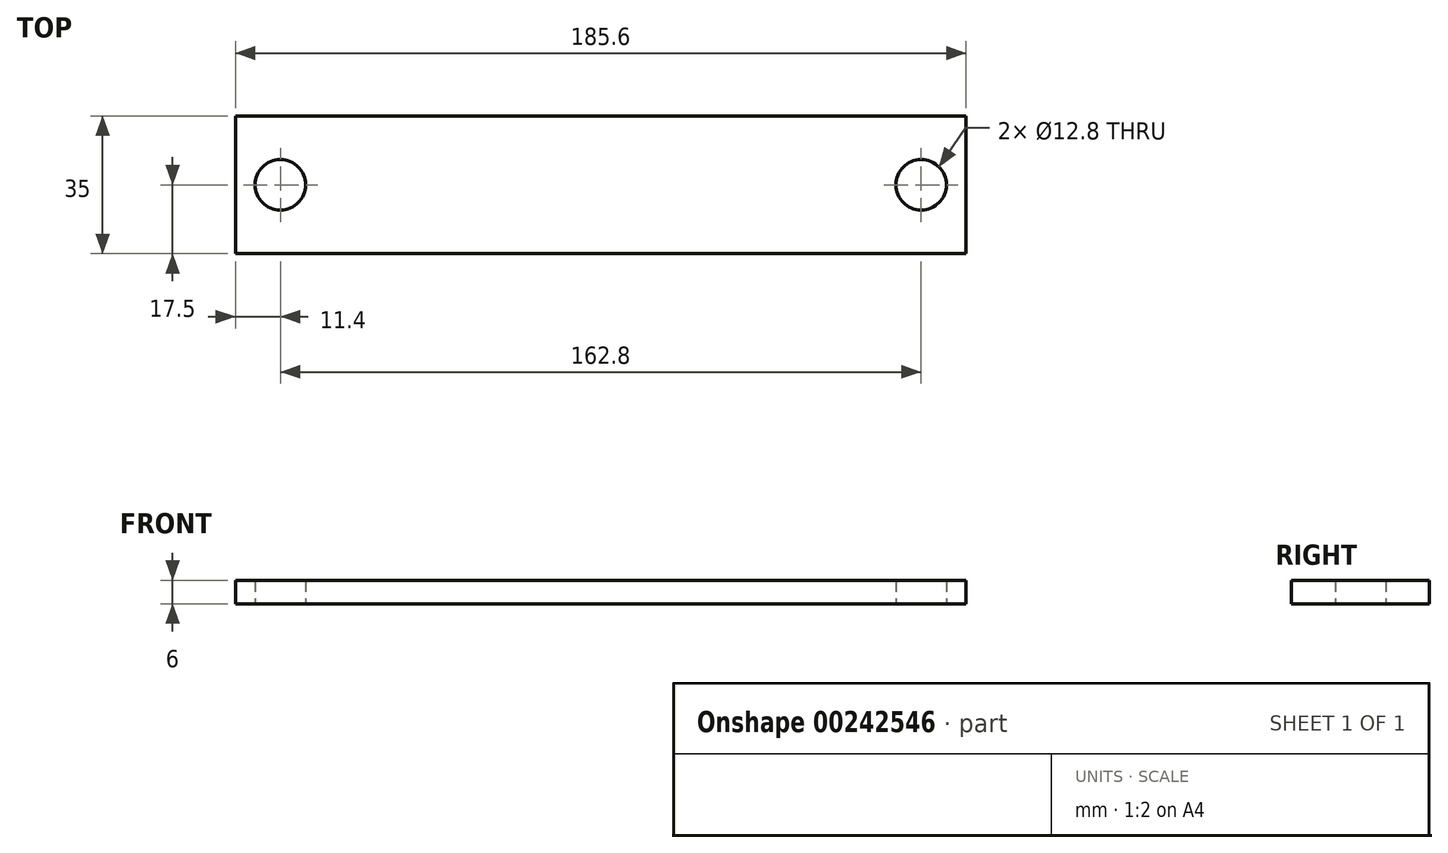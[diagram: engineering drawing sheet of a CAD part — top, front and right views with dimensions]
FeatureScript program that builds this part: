
annotation { "Feature Type Name" : "Feature", "Feature Type Description" : "" }
export const myFeature = defineFeature(function(context is Context, id is Id, definition is map)
    precondition{}
    {
        {
            var Q0;
            Q0=qCreatedBy(makeId("Top.planeOp"),FACE);
            var sketch = newSketch(context, id + "F0", { "sketchPlane" : qUnion([Q0])});
            skLineSegment(sketch, "E0.bottom", {"start": v(92.8, -17.5) * mm, "end": v(-92.8, -17.5) * mm});
            skLineSegment(sketch, "E0.top", {"start": v(92.8, 17.5) * mm, "end": v(-92.8, 17.5) * mm});
            skLineSegment(sketch, "E0.left", {"start": v(92.8, -17.5) * mm, "end": v(92.8, 17.5) * mm});
            skLineSegment(sketch, "E0.right", {"start": v(-92.8, -17.5) * mm, "end": v(-92.8, 17.5) * mm});
            skPoint(sketch, "E0.middle", {"position": v(0, 0) * mm});
            skCircle(sketch, "E1", {"center": v(-81.4, 0) * mm, "radius": 6.4 * mm});
            skCircle(sketch, "E2", {"center": v(81.4, 0) * mm, "radius": 6.4 * mm});
            skSolve(sketch);
        }
        {
            var Q0;
            Q0=makeQuery(id+"F0.imprint","IMPRINT",FACE,{"disambiguationData":[TD([[makeQuery(id+"F0.imprint","IMPRINT",EDGE,{"derivedFrom":sQuery(id+"F0.wireOp",EDGE,"E0.bottom")}),-1.0]])]});
            extrude(context, id + "F1", {"entities" : qUnion([Q0]), "depth" : 6 * mm});
        }
    });
